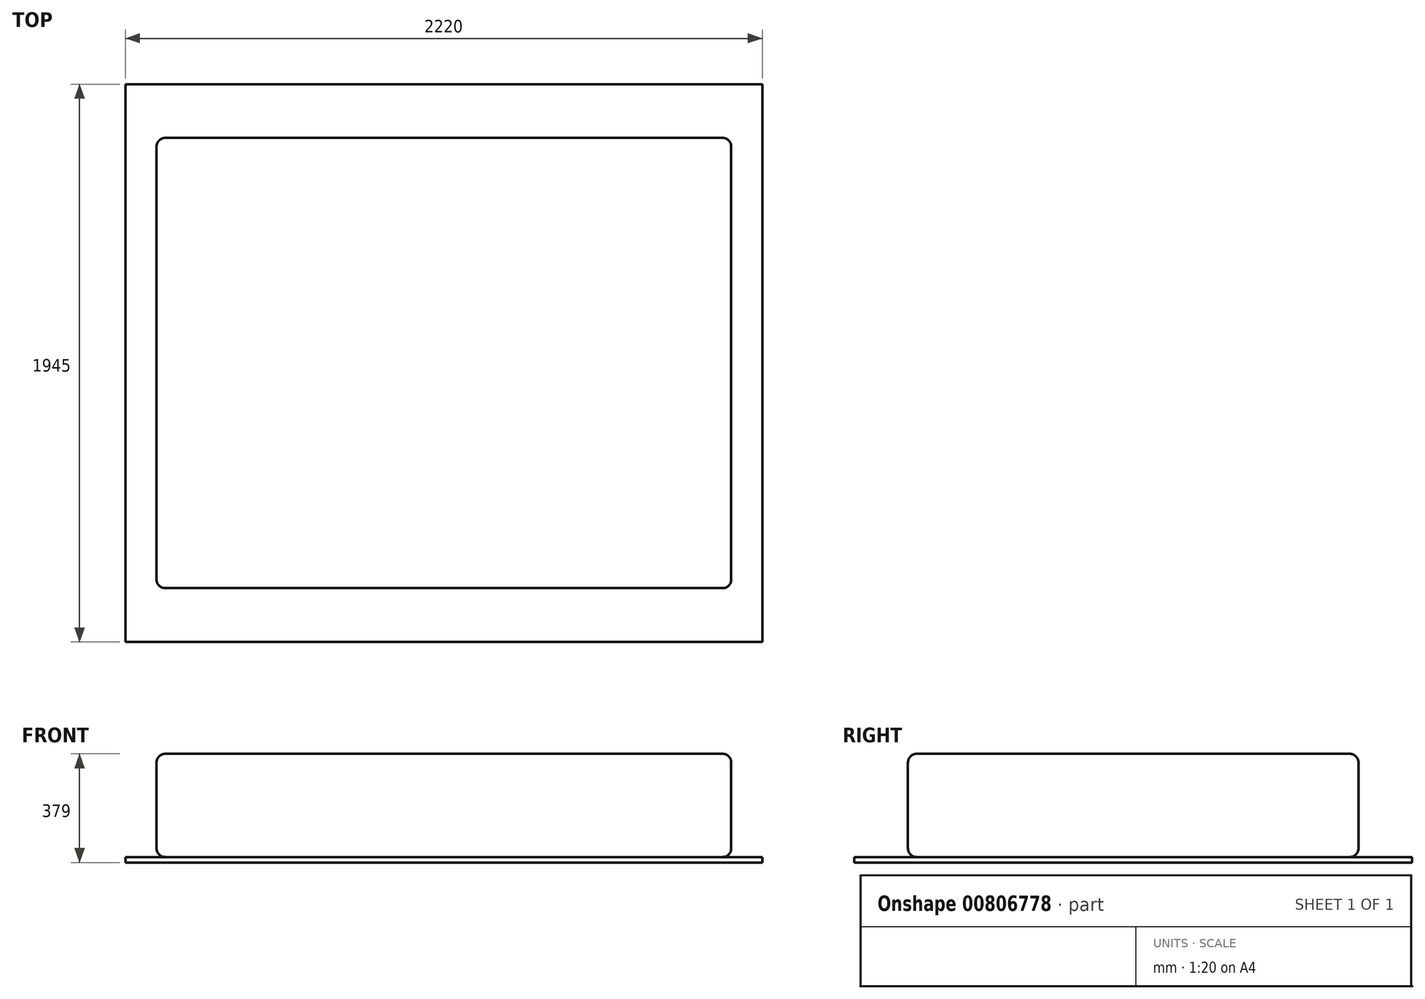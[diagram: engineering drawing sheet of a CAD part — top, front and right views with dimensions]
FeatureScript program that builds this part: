
annotation { "Feature Type Name" : "Feature", "Feature Type Description" : "" }
export const myFeature = defineFeature(function(context is Context, id is Id, definition is map)
    precondition{}
    {
        {
            var Q0;
            Q0=qCreatedBy(makeId("Top.planeOp"),FACE);
            var sketch = newSketch(context, id + "F0", { "sketchPlane" : qUnion([Q0])});
            skLineSegment(sketch, "E0.bottom", {"start": v(1110, 972.5) * mm, "end": v(-1110, 972.5) * mm});
            skLineSegment(sketch, "E0.top", {"start": v(1110, -972.5) * mm, "end": v(-1110, -972.5) * mm});
            skLineSegment(sketch, "E0.left", {"start": v(1110, 972.5) * mm, "end": v(1110, -972.5) * mm});
            skLineSegment(sketch, "E0.right", {"start": v(-1110, 972.5) * mm, "end": v(-1110, -972.5) * mm});
            skPoint(sketch, "E0.middle", {"position": v(0, 0) * mm});
            skSolve(sketch);
        }
        {
            var Q0;
            Q0=makeQuery(id+"F0.imprint","IMPRINT",FACE,{"disambiguationData":[TD([[makeQuery(id+"F0.imprint","IMPRINT",EDGE,{"derivedFrom":sQuery(id+"F0.wireOp",EDGE,"E0.bottom")}),1.0]])]});
            extrude(context, id + "F1", {"entities" : qUnion([Q0]), "depth" : 19 * mm, "offsetDistance" : 25 * mm});
        }
        {
            var Q0;
            Q0=makeQuery(id+"F1.opExtrude","CAP_FACE",FACE,{"disambiguationData":[OSD([sQuery(id+"F0.wireOp",EDGE,"E0.bottom"),sQuery(id+"F0.wireOp",EDGE,"E0.top"),sQuery(id+"F0.wireOp",EDGE,"E0.left"),sQuery(id+"F0.wireOp",EDGE,"E0.right")])],"isStart":false});
            var sketch = newSketch(context, id + "F2", { "sketchPlane" : qUnion([Q0])});
            skLineSegment(sketch, "E1.bottom", {"start": v(1001.5, 785) * mm, "end": v(-1001.5, 785) * mm});
            skLineSegment(sketch, "E1.top", {"start": v(1001.5, -785) * mm, "end": v(-1001.5, -785) * mm});
            skLineSegment(sketch, "E1.left", {"start": v(1001.5, 785) * mm, "end": v(1001.5, -785) * mm});
            skLineSegment(sketch, "E1.right", {"start": v(-1001.5, 785) * mm, "end": v(-1001.5, -785) * mm});
            skPoint(sketch, "E1.middle", {"position": v(0, 0) * mm});
            skSolve(sketch);
        }
        {
            var Q0;
            Q0=makeQuery(id+"F2.imprint","IMPRINT",FACE,{"disambiguationData":[TD([[makeQuery(id+"F2.imprint","IMPRINT",EDGE,{"derivedFrom":sQuery(id+"F2.wireOp",EDGE,"E1.bottom")}),1.0]])]});
            extrude(context, id + "F3", {"entities" : qUnion([Q0]), "depth" : 360 * mm, "offsetDistance" : 25 * mm});
        }
        {
            var Q0;
            Q0=makeQuery(id+"F3.opExtrude","CAP_FACE",FACE,{"disambiguationData":[OSD([sQuery(id+"F2.wireOp",EDGE,"E1.bottom"),sQuery(id+"F2.wireOp",EDGE,"E1.top"),sQuery(id+"F2.wireOp",EDGE,"E1.left"),sQuery(id+"F2.wireOp",EDGE,"E1.right")])],"isStart":false});
            var Q1;
            Q1=makeQuery(id+"F3.opExtrude","SWEPT_EDGE",EDGE,{"disambiguationData":[OSD([sQuery(id+"F2.wireOp",EDGE,"E1.top"),sQuery(id+"F2.wireOp",EDGE,"E1.right")])]});
            var Q2;
            Q2=makeQuery(id+"F3.opExtrude","CAP_EDGE",EDGE,{"disambiguationData":[OSD([sQuery(id+"F2.wireOp",EDGE,"E1.top")])],"isStart":true});
            var Q3;
            Q3=makeQuery(id+"F3.opExtrude","CAP_EDGE",EDGE,{"disambiguationData":[OSD([sQuery(id+"F2.wireOp",EDGE,"E1.right")])],"isStart":true});
            var Q4;
            Q4=makeQuery(id+"F3.opExtrude","SWEPT_EDGE",EDGE,{"disambiguationData":[OSD([sQuery(id+"F2.wireOp",EDGE,"E1.bottom"),sQuery(id+"F2.wireOp",EDGE,"E1.right")])]});
            var Q5;
            Q5=makeQuery(id+"F3.opExtrude","CAP_EDGE",EDGE,{"disambiguationData":[OSD([sQuery(id+"F2.wireOp",EDGE,"E1.bottom")])],"isStart":true});
            var Q6;
            Q6=makeQuery(id+"F3.opExtrude","SWEPT_EDGE",EDGE,{"disambiguationData":[OSD([sQuery(id+"F2.wireOp",EDGE,"E1.bottom"),sQuery(id+"F2.wireOp",EDGE,"E1.left")])]});
            var Q7;
            Q7=makeQuery(id+"F3.opExtrude","CAP_EDGE",EDGE,{"disambiguationData":[OSD([sQuery(id+"F2.wireOp",EDGE,"E1.left")])],"isStart":true});
            var Q8;
            Q8=makeQuery(id+"F3.opExtrude","SWEPT_EDGE",EDGE,{"disambiguationData":[OSD([sQuery(id+"F2.wireOp",EDGE,"E1.top"),sQuery(id+"F2.wireOp",EDGE,"E1.left")])]});
            fillet(context, id + "F4", {"entities" : qUnion([Q0, Q1, Q2, Q3, Q4, Q5, Q6, Q7, Q8]), "radius" : 30 * mm, "tangentPropagation" : true, "allowEdgeOverflow" : false});
        }
    });
